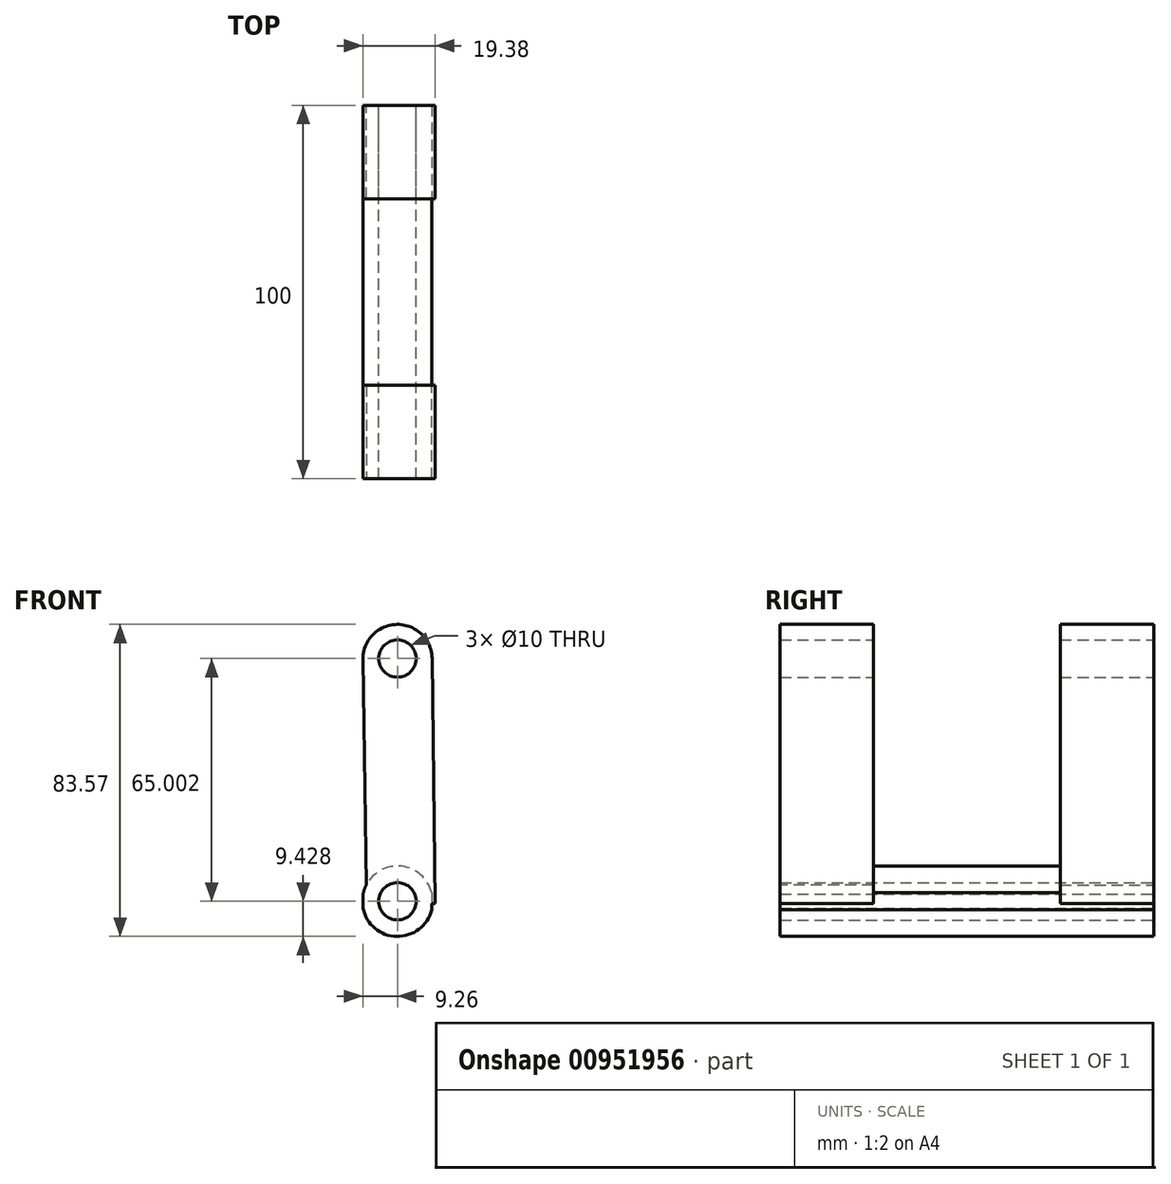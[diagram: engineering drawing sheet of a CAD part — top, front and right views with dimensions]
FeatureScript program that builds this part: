
annotation { "Feature Type Name" : "Feature", "Feature Type Description" : "" }
export const myFeature = defineFeature(function(context is Context, id is Id, definition is map)
    precondition{}
    {
        {
            var Q0;
            Q0=qCreatedBy(makeId("Front.planeOp"),FACE);
            var sketch = newSketch(context, id + "F0", { "sketchPlane" : qUnion([Q0])});
            skCircle(sketch, "E0", {"center": v(0, -21.28) * mm, "radius": 9.42 * mm});
            skCircle(sketch, "E1", {"center": v(0, 39.27) * mm, "radius": 9.24 * mm});
            skLineSegment(sketch, "E2", {"start": v(-9.23, 39.7) * mm, "end": v(-9.23, -23.18) * mm});
            skLineSegment(sketch, "E3", {"start": v(9.15, 40.55) * mm, "end": v(9.15, -23.53) * mm});
            skSolve(sketch);
        }
        {
            var Q0;
            {var subQ0=sQuery(id+"F0.wireOp",EDGE,"E2");var subQ1=sQuery(id+"F0.wireOp",EDGE,"E0");var subQ2=makeQuery(id+"F0.imprint","INTERSECT",VERTEX,{"disambiguationData":[OD(1.0)],"derivedFrom":[subQ1,subQ0]});Q0=makeQuery(id+"F0.imprint","IMPRINT",FACE,{"disambiguationData":[TD([[makeQuery(id+"F0.imprint","IMPRINT",EDGE,{"disambiguationData":[TD([[subQ2,1.0]])],"derivedFrom":subQ1}),1.0]])]});}
            extrude(context, id + "F1", {"entities" : qUnion([Q0]), "depth" : 50 * mm, "offsetDistance" : 25 * mm});
        }
        {
            var Q0;
            Q0=qCreatedBy(makeId("Front.planeOp"),FACE);
            var sketch = newSketch(context, id + "F2", { "sketchPlane" : qUnion([Q0])});
            skCircle(sketch, "E4", {"center": v(0, 43.6) * mm, "radius": 9.26 * mm});
            skLineSegment(sketch, "E5", {"start": v(-9.26, 43.46) * mm, "end": v(-8.26, -21.85) * mm});
            skLineSegment(sketch, "E6", {"start": v(-8.26, -21.85) * mm, "end": v(10.12, -21.85) * mm});
            skLineSegment(sketch, "E7", {"start": v(10.12, -21.85) * mm, "end": v(9.26, 43.72) * mm});
            skSolve(sketch);
        }
        {
            var Q0;
            {var subQ0=sQuery(id+"F2.wireOp",EDGE,"E5");Q0=makeQuery(id+"F2.imprint","IMPRINT",FACE,{"disambiguationData":[TD([[makeQuery(id+"F2.imprint","IMPRINT",EDGE,{"derivedFrom":subQ0}),1.0]])]});}
            var Q1;
            {var subQ0=sQuery(id+"F2.wireOp",EDGE,"E4");var subQ1=makeQuery(id+"F2.imprint","INTERSECT",VERTEX,{"derivedFrom":[subQ0,sQuery(id+"F2.wireOp",EDGE,"E5")]});Q1=makeQuery(id+"F2.imprint","IMPRINT",FACE,{"disambiguationData":[TD([[makeQuery(id+"F2.imprint","IMPRINT",EDGE,{"disambiguationData":[TD([[subQ1,1.0]])],"derivedFrom":subQ0}),1.0]])]});}
            extrude(context, id + "F3", {"entities" : qUnion([Q0, Q1]), "operationType" : NewBodyOperationType.ADD, "depth" : 25 * mm, "offsetDistance" : 25 * mm});
        }
        {
            var Q0;
            Q0=makeQuery(id+"F1.opExtrude","SWEPT_BODY",BODY,{"disambiguationData":[OSD([sQuery(id+"F0.wireOp",EDGE,"E0"),sQuery(id+"F0.wireOp",EDGE,"E2"),sQuery(id+"F0.wireOp",EDGE,"E3")])]});
            var Q1;
            Q1=makeQuery(id+"F1.opExtrude","CAP_FACE",FACE,{"disambiguationData":[OSD([sQuery(id+"F0.wireOp",EDGE,"E0"),sQuery(id+"F0.wireOp",EDGE,"E2"),sQuery(id+"F0.wireOp",EDGE,"E3")])],"isStart":false});
            mirror(context, id + "F4", {"operationType" : NewBodyOperationType.ADD, "entities" : qUnion([Q0]), "mirrorPlane" : qUnion([Q1])});
        }
        {
            var Q0;
            Q0=makeQuery(id+"F3.boolean.opBoolean","MERGE",FACE,{"derivedFrom":[makeQuery(id+"F1.opExtrude","CAP_FACE",FACE,{"disambiguationData":[OSD([sQuery(id+"F0.wireOp",EDGE,"E0"),sQuery(id+"F0.wireOp",EDGE,"E2"),sQuery(id+"F0.wireOp",EDGE,"E3")])],"isStart":true}),makeQuery(id+"F3.opExtrude","CAP_FACE",FACE,{"disambiguationData":[OSD([sQuery(id+"F2.wireOp",EDGE,"E4"),sQuery(id+"F2.wireOp",EDGE,"E5"),sQuery(id+"F2.wireOp",EDGE,"E6"),sQuery(id+"F2.wireOp",EDGE,"E7")])],"isStart":true})]});
            var sketch = newSketch(context, id + "F5", { "sketchPlane" : qUnion([Q0])});
            skCircle(sketch, "E8", {"center": v(0, 43.72) * mm, "radius": 3.58 * mm});
            skCircle(sketch, "E9", {"center": v(0, -21.28) * mm, "radius": 4.57 * mm});
            skSolve(sketch);
        }
        {
            var Q0;
            Q0=sQuery(id+"F5.wireOp",VERTEX,"E8.center");
            var Q1;
            Q1=sQuery(id+"F5.wireOp",VERTEX,"E9.center");
            var Q2;
            Q2=makeQuery(id+"F1.opExtrude","SWEPT_BODY",BODY,{"disambiguationData":[OSD([sQuery(id+"F0.wireOp",EDGE,"E0"),sQuery(id+"F0.wireOp",EDGE,"E2"),sQuery(id+"F0.wireOp",EDGE,"E3")])]});
            hole(context, id + "F6", {"style" : HoleStyle.SIMPLE, "endStyle" : HoleEndStyle.THROUGH, "holeDiameter" : 10 * mm, "majorDiameter" : 5 * mm, "isTappedThrough" : true, "tappedDepth" : 12 * mm, "tapClearance" : 3, "locations" : qUnion([Q0, Q1]), "scope" : qUnion([Q2])});
        }
    });
